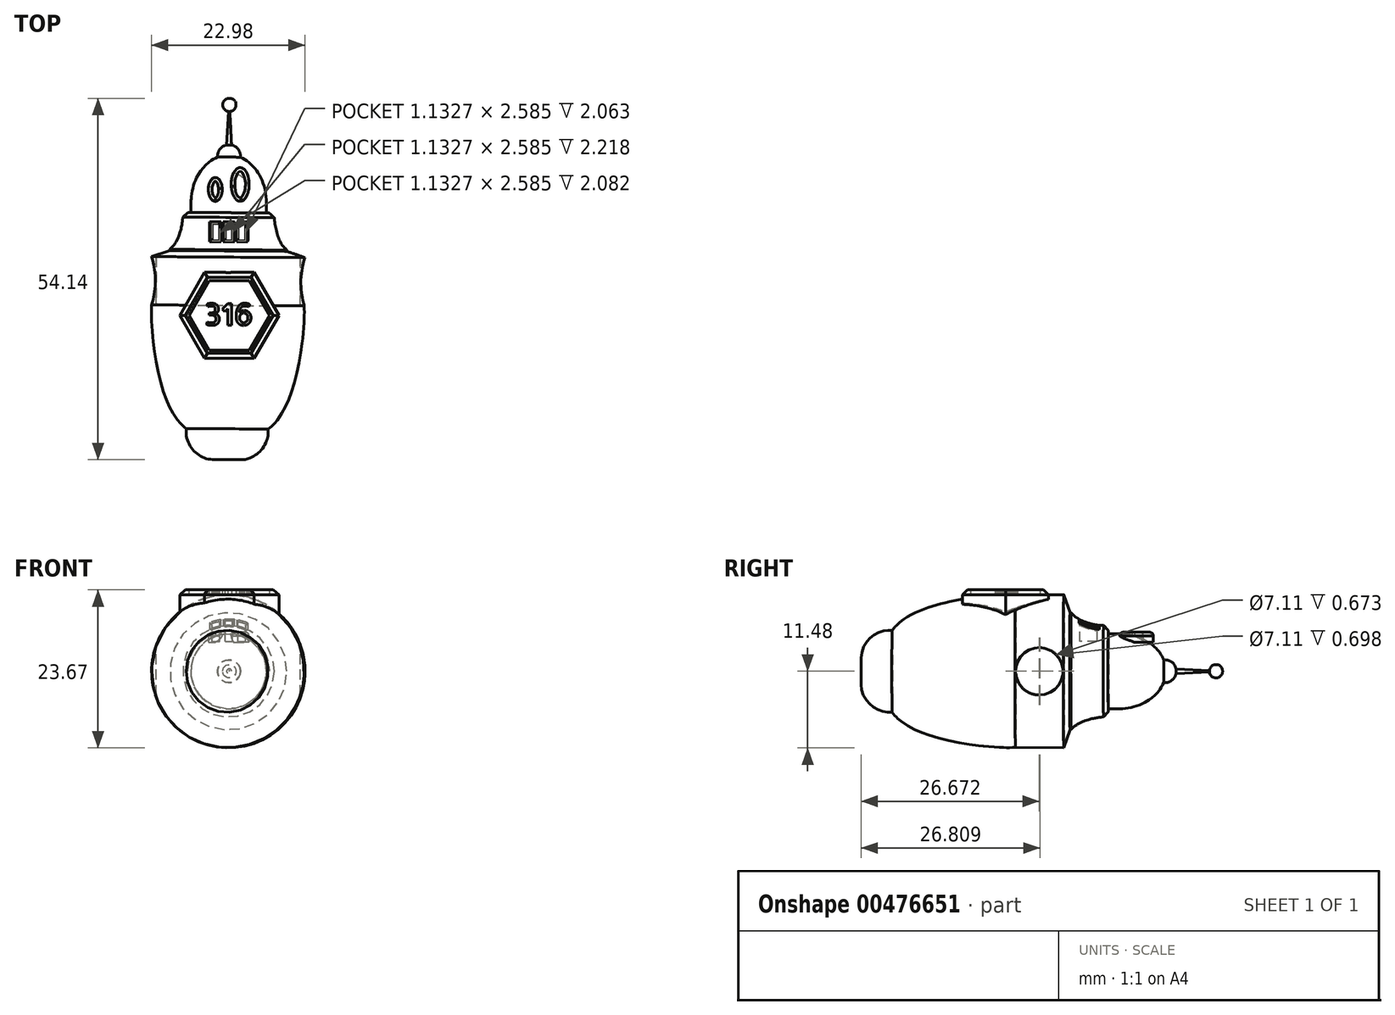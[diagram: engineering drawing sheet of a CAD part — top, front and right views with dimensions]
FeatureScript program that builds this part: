
annotation { "Feature Type Name" : "Feature", "Feature Type Description" : "" }
export const myFeature = defineFeature(function(context is Context, id is Id, definition is map)
    precondition{}
    {
        {
            var Q0;
            Q0=qCreatedBy(makeId("Top.planeOp"),FACE);
            var sketch = newSketch(context, id + "F0", { "sketchPlane" : qUnion([Q0])});
            skLineSegment(sketch, "E0", {"start": v(-10.48, 12.63) * mm, "end": v(-10.48, 19.87) * mm});
            skFitSpline(sketch, "E1", {"points": [v(10.09, 20.95) * mm, v(10.15, 21.01) * mm], "startDerivative": vector(0.06, 0.06) * mm, "endDerivative": vector(0.06, 0.06) * mm});
            skFitSpline(sketch, "E2", {"points": [v(-7.76, 20.95) * mm, v(-7.24, 21.45) * mm, v(-6.6, 22.5) * mm, v(-6.03, 24.25) * mm, v(-5.81, 25.75) * mm, v(-5.77, 26.5) * mm], "startDerivative": vector(3.3, 2.83) * mm, "endDerivative": vector(0.16, 4.27) * mm});
            skLineSegment(sketch, "E3", {"start": v(-10.48, 19.87) * mm, "end": v(-7.76, 20.79) * mm});
            skLineSegment(sketch, "E4", {"start": v(-7.76, 20.79) * mm, "end": v(-7.76, 20.95) * mm});
            skLineSegment(sketch, "E5", {"start": v(-5.77, 26.5) * mm, "end": v(-4.58, 26.5) * mm});
            skFitSpline(sketch, "E6", {"points": [v(-4.58, 26.5) * mm, v(-4.58, 27.5) * mm, v(-4.5, 29.13) * mm, v(-4, 31.1) * mm, v(-3.35, 32.38) * mm, v(-2.49, 33.48) * mm, v(-1.51, 34.3) * mm, v(-0.6, 34.79) * mm], "startDerivative": vector(0, 7.8) * mm, "endDerivative": vector(7.4, 3.58) * mm});
            skFitSpline(sketch, "E7", {"points": [v(-0.6, 34.79) * mm, v(-0.6, 35.1) * mm, v(-0.49, 35.58) * mm, v(-0.23, 36) * mm, v(0.1, 36.33) * mm, v(0.49, 36.52) * mm, v(0.75, 36.6) * mm], "startDerivative": vector(-0.1, 2.05) * mm, "endDerivative": vector(1.87, 0.4) * mm});
            skPoint(sketch, "E8.endSnap0", {"position": v(1.17, 21.6) * mm});
            skLineSegment(sketch, "E9", {"start": v(0.75, 36.6) * mm, "end": v(1.07, 41.6) * mm});
            skFitSpline(sketch, "E10", {"points": [v(1.07, 41.6) * mm, v(0.8, 41.67) * mm, v(0.53, 41.82) * mm, v(0.33, 42.03) * mm, v(0.2, 42.3) * mm, v(0.17, 42.5) * mm, v(0.16, 42.76) * mm, v(0.2, 42.94) * mm, v(0.31, 43.15) * mm, v(0.5, 43.35) * mm, v(0.66, 43.48) * mm, v(0.83, 43.54) * mm, v(1.04, 43.57) * mm, v(1.17, 43.57) * mm], "startDerivative": vector(-3.3, 0.6) * mm, "endDerivative": vector(2, -0.06) * mm});
            skFitSpline(sketch, "E11", {"points": [v(-10.48, 12.63) * mm, v(-10.48, 10.12) * mm, v(-10.15, 6.52) * mm, v(-9.38, 2.07) * mm, v(-7.68, -2.9) * mm, v(-6, -5.3) * mm, v(-5.29, -5.89) * mm], "startDerivative": vector(-0.37, -16.05) * mm, "endDerivative": vector(7.16, -5.3) * mm});
            skFitSpline(sketch, "E12", {"points": [v(-5.29, -5.89) * mm, v(-5.29, -6.9) * mm, v(-4.86, -8.2) * mm, v(-4.1, -9.28) * mm, v(-3.04, -10.07) * mm, v(-1.85, -10.48) * mm, v(-0.47, -10.54) * mm, v(0.8, -10.54) * mm], "startDerivative": vector(-0.6, -7.63) * mm, "endDerivative": vector(8.74, -0.05) * mm});
            skLineSegment(sketch, "E13", {"start": v(0.8, -10.54) * mm, "end": v(1.17, 43.57) * mm});
            skSolve(sketch);
        }
        {
            var Q0;
            Q0 = qSketchRegion(id + "F0", true);
            var Q1;
            Q1=sQuery(id+"F0.wireOp",EDGE,"E13");
            revolve(context, id + "F1", {"entities" : qUnion([Q0]), "axis" : qUnion([Q1]), "revolveType" : RevolveType.FULL});
        }
        {
            var Q0;
            Q0=qCreatedBy(makeId("Top.planeOp"),FACE);
            var Q1;
            Q1 = qBodyType(qCreatedBy(id + "F3" ,EDGE), BodyType.WIRE);
            cPlane(context, id + "F2", {"entities" : qUnion([Q0, Q1]), "cplaneType" : CPlaneType.OFFSET, "offset" : 5.08 * mm, "width" : 152.4 * mm, "height" : 152.4 * mm});
        }
        {
            var Q0;
            Q0=qCreatedBy(id+"F2.planeOp",FACE);
            var sketch = newSketch(context, id + "F3", { "sketchPlane" : qUnion([Q0])});
            skEllipse(sketch, "E14", {"center": v(-0.95, 29.94) * mm, "majorRadius": 1.78 * mm, "minorRadius": 1.04 * mm, "majorAxis": v(0, -1)});
            skEllipse(sketch, "E15", {"center": v(2.78, 30.68) * mm, "majorRadius": 2.53 * mm, "minorRadius": 1.34 * mm, "majorAxis": v(0, 1)});
            skPoint(sketch, "E16.endSnap0", {"position": v(-0.95, 28.16) * mm});
            skSolve(sketch);
        }
        {
            var Q0;
            Q0 = qSketchRegion(id + "F3", true);
            extrude(context, id + "F4", {"entities" : qUnion([Q0]), "operationType" : NewBodyOperationType.ADD, "endBound" : BoundingType.SYMMETRIC, "depth" : 1.52 * mm});
        }
        {
            var Q0;
            Q0=makeQuery(id+"F4.opExtrude","CAP_EDGE",EDGE,{"disambiguationData":[OSD([sQuery(id+"F3.wireOp",EDGE,"E15")])],"isStart":false});
            var Q1;
            Q1=makeQuery(id+"F4.opExtrude","CAP_EDGE",EDGE,{"disambiguationData":[OSD([sQuery(id+"F3.wireOp",EDGE,"E14")])],"isStart":false});
            fillet(context, id + "F5", {"entities" : qUnion([Q0, Q1]), "radius" : 0.55 * mm, "tangentPropagation" : true, "allowEdgeOverflow" : false});
        }
        {
            var Q0;
            Q0=qCreatedBy(makeId("Top.planeOp"),FACE);
            cPlane(context, id + "F6", {"entities" : qUnion([Q0]), "cplaneType" : CPlaneType.OFFSET, "offset" : 6.35 * mm, "width" : 152.4 * mm, "height" : 152.4 * mm});
        }
        {
            var Q0;
            Q0=qCreatedBy(id+"F6.planeOp",FACE);
            var sketch = newSketch(context, id + "F7", { "sketchPlane" : qUnion([Q0])});
            skLineSegment(sketch, "E17.bottom", {"start": v(-1.44, 24.82) * mm, "end": v(-0.31, 24.82) * mm});
            skLineSegment(sketch, "E17.top", {"start": v(-1.44, 22.23) * mm, "end": v(-0.31, 22.23) * mm});
            skLineSegment(sketch, "E17.left", {"start": v(-1.44, 24.82) * mm, "end": v(-1.44, 22.23) * mm});
            skLineSegment(sketch, "E17.right", {"start": v(-0.31, 24.82) * mm, "end": v(-0.31, 22.23) * mm});
            skLineSegment(sketch, "E18.1.0.0", {"start": v(1.65, 24.82) * mm, "end": v(1.65, 22.23) * mm});
            skLineSegment(sketch, "E18.1.0.1", {"start": v(0.51, 24.82) * mm, "end": v(1.65, 24.82) * mm});
            skLineSegment(sketch, "E18.1.0.2", {"start": v(0.51, 24.82) * mm, "end": v(0.51, 22.23) * mm});
            skLineSegment(sketch, "E18.1.0.3", {"start": v(0.51, 22.23) * mm, "end": v(1.65, 22.23) * mm});
            skLineSegment(sketch, "E18.2.0.0", {"start": v(3.6, 24.82) * mm, "end": v(3.6, 22.23) * mm});
            skLineSegment(sketch, "E18.2.0.1", {"start": v(2.47, 24.82) * mm, "end": v(3.6, 24.82) * mm});
            skLineSegment(sketch, "E18.2.0.2", {"start": v(2.47, 24.82) * mm, "end": v(2.47, 22.23) * mm});
            skLineSegment(sketch, "E18.2.0.3", {"start": v(2.47, 22.23) * mm, "end": v(3.6, 22.23) * mm});
            skLineSegment(sketch, "E18.direction1", {"start": v(-0.31, 22.23) * mm, "end": v(1.65, 22.23) * mm, "construction": true});
            skSolve(sketch);
        }
        {
            var Q0;
            Q0 = qSketchRegion(id + "F7", true);
            extrude(context, id + "F8", {"entities" : qUnion([Q0]), "operationType" : NewBodyOperationType.REMOVE, "endBound" : BoundingType.SYMMETRIC, "oppositeDirection" : true, "depth" : 3.8 * mm});
        }
        {
            var Q0;
            Q0=qCreatedBy(makeId("Top.planeOp"),FACE);
            cPlane(context, id + "F9", {"entities" : qUnion([Q0]), "cplaneType" : CPlaneType.OFFSET, "offset" : 7.62 * mm, "width" : 152.4 * mm, "height" : 152.4 * mm});
        }
        {
            var Q0;
            Q0=qCreatedBy(id+"F9.planeOp",FACE);
            var sketch = newSketch(context, id + "F10", { "sketchPlane" : qUnion([Q0])});
            skCircle(sketch, "E19.cCircle", {"center": v(1.17, 11.07) * mm, "radius": 6.45 * mm, "construction": true});
            skLineSegment(sketch, "E19.0", {"start": v(-2.55, 17.52) * mm, "end": v(4.9, 17.52) * mm});
            skLineSegment(sketch, "E19.1", {"start": v(4.9, 17.52) * mm, "end": v(8.61, 11.07) * mm});
            skLineSegment(sketch, "E19.2", {"start": v(8.61, 11.07) * mm, "end": v(4.9, 4.62) * mm});
            skLineSegment(sketch, "E19.3", {"start": v(4.9, 4.62) * mm, "end": v(-2.55, 4.62) * mm});
            skLineSegment(sketch, "E19.4", {"start": v(-2.55, 4.62) * mm, "end": v(-6.28, 11.07) * mm});
            skLineSegment(sketch, "E19.5", {"start": v(-6.28, 11.07) * mm, "end": v(-2.55, 17.52) * mm});
            skPoint(sketch, "E19.0.midPoint", {"position": v(1.17, 17.52) * mm});
            skSolve(sketch);
        }
        {
            var Q0;
            Q0 = qSketchRegion(id + "F10", true);
            extrude(context, id + "F11", {"entities" : qUnion([Q0]), "operationType" : NewBodyOperationType.ADD, "depth" : 4.57 * mm});
        }
        {
            var Q0;
            Q0=makeQuery(id+"F11.opExtrude","CAP_FACE",FACE,{"disambiguationData":[OSD([sQuery(id+"F10.wireOp",EDGE,"E19.0"),sQuery(id+"F10.wireOp",EDGE,"E19.1"),sQuery(id+"F10.wireOp",EDGE,"E19.2"),sQuery(id+"F10.wireOp",EDGE,"E19.3"),sQuery(id+"F10.wireOp",EDGE,"E19.4"),sQuery(id+"F10.wireOp",EDGE,"E19.5")])],"isStart":false});
            var sketch = newSketch(context, id + "F12", { "sketchPlane" : qUnion([Q0])});
            skCircle(sketch, "E20.cCircle", {"center": v(1.17, 11.07) * mm, "radius": 5.21 * mm, "construction": true});
            skPoint(sketch, "E20.cCircle.centerSnap0", {"position": v(1.17, 17.52) * mm});
            skLineSegment(sketch, "E20.0", {"start": v(-1.84, 16.28) * mm, "end": v(4.18, 16.28) * mm});
            skLineSegment(sketch, "E20.1", {"start": v(4.18, 16.28) * mm, "end": v(7.19, 11.07) * mm});
            skLineSegment(sketch, "E20.2", {"start": v(7.19, 11.07) * mm, "end": v(4.18, 5.86) * mm});
            skLineSegment(sketch, "E20.3", {"start": v(4.18, 5.86) * mm, "end": v(-1.84, 5.86) * mm});
            skLineSegment(sketch, "E20.4", {"start": v(-1.84, 5.86) * mm, "end": v(-4.85, 11.07) * mm});
            skLineSegment(sketch, "E20.5", {"start": v(-4.85, 11.07) * mm, "end": v(-1.84, 16.28) * mm});
            skPoint(sketch, "E20.0.midPoint", {"position": v(1.17, 16.28) * mm});
            skSolve(sketch);
        }
        {
            var Q0;
            Q0 = qSketchRegion(id + "F12", true);
            extrude(context, id + "F13", {"entities" : qUnion([Q0]), "operationType" : NewBodyOperationType.REMOVE, "oppositeDirection" : true, "depth" : 0.76 * mm});
        }
        {
            var Q0;
            Q0=makeQuery(id+"F11.opExtrude","CAP_EDGE",EDGE,{"disambiguationData":[OSD([sQuery(id+"F10.wireOp",EDGE,"E19.5")])],"isStart":false});
            var Q1;
            Q1=makeQuery(id+"F11.opExtrude","CAP_EDGE",EDGE,{"disambiguationData":[OSD([sQuery(id+"F10.wireOp",EDGE,"E19.4")])],"isStart":false});
            var Q2;
            Q2=makeQuery(id+"F11.opExtrude","CAP_EDGE",EDGE,{"disambiguationData":[OSD([sQuery(id+"F10.wireOp",EDGE,"E19.3")])],"isStart":false});
            var Q3;
            Q3=makeQuery(id+"F11.opExtrude","CAP_EDGE",EDGE,{"disambiguationData":[OSD([sQuery(id+"F10.wireOp",EDGE,"E19.0")])],"isStart":false});
            var Q4;
            Q4=makeQuery(id+"F11.opExtrude","CAP_EDGE",EDGE,{"disambiguationData":[OSD([sQuery(id+"F10.wireOp",EDGE,"E19.1")])],"isStart":false});
            var Q5;
            Q5=makeQuery(id+"F11.opExtrude","CAP_EDGE",EDGE,{"disambiguationData":[OSD([sQuery(id+"F10.wireOp",EDGE,"E19.2")])],"isStart":false});
            chamfer(context, id + "F14", {"entities" : qUnion([Q0, Q1, Q2, Q3, Q4, Q5]), "width" : 0.76 * mm, "tangentPropagation" : true});
        }
        {
            var Q0;
            Q0=makeQuery(id+"F13.boolean.opBoolean","COPY",FACE,{"derivedFrom":makeQuery(id+"F13.opExtrude","CAP_FACE",FACE,{"disambiguationData":[OSD([sQuery(id+"F12.wireOp",EDGE,"E20.0"),sQuery(id+"F12.wireOp",EDGE,"E20.1"),sQuery(id+"F12.wireOp",EDGE,"E20.2"),sQuery(id+"F12.wireOp",EDGE,"E20.3"),sQuery(id+"F12.wireOp",EDGE,"E20.4"),sQuery(id+"F12.wireOp",EDGE,"E20.5")])],"isStart":false})});
            var sketch = newSketch(context, id + "F15", { "sketchPlane" : qUnion([Q0])});
            skText(sketch, "E21", { "text": "316", "fontName": "AllertaStencil-Regular.ttf"});
            const initialGuessF15  = {"E21": [-0.0026, 0.00958, 1, 0, 0.00328]};
            skSetInitialGuess(sketch, initialGuessF15);
            skSolve(sketch);
        }
        {
            var Q0;
            Q0 = qSketchRegion(id + "F15", true);
            extrude(context, id + "F16", {"entities" : qUnion([Q0]), "operationType" : NewBodyOperationType.ADD, "depth" : 0.76 * mm});
        }
        {
            var Q0;
            Q0=makeQuery(id+"F8.boolean.opBoolean","INTERSECT",EDGE,{"derivedFrom":[makeQuery(id+"F1.opRevolve","SWEPT_FACE",FACE,{"disambiguationData":[OSD([sQuery(id+"F0.wireOp",EDGE,"E2")])]}),makeQuery(id+"F8.opExtrude","SWEPT_FACE",FACE,{"disambiguationData":[OSD([sQuery(id+"F7.wireOp",EDGE,"E17.bottom")])]})]});
            var Q1;
            Q1=makeQuery(id+"F8.boolean.opBoolean","INTERSECT",EDGE,{"derivedFrom":[makeQuery(id+"F1.opRevolve","SWEPT_FACE",FACE,{"disambiguationData":[OSD([sQuery(id+"F0.wireOp",EDGE,"E2")])]}),makeQuery(id+"F8.opExtrude","SWEPT_FACE",FACE,{"disambiguationData":[OSD([sQuery(id+"F7.wireOp",EDGE,"E17.right")])]})]});
            var Q2;
            Q2=makeQuery(id+"F8.boolean.opBoolean","INTERSECT",EDGE,{"derivedFrom":[makeQuery(id+"F1.opRevolve","SWEPT_FACE",FACE,{"disambiguationData":[OSD([sQuery(id+"F0.wireOp",EDGE,"E2")])]}),makeQuery(id+"F8.opExtrude","SWEPT_FACE",FACE,{"disambiguationData":[OSD([sQuery(id+"F7.wireOp",EDGE,"E17.top")])]})]});
            var Q3;
            Q3=makeQuery(id+"F8.boolean.opBoolean","INTERSECT",EDGE,{"derivedFrom":[makeQuery(id+"F1.opRevolve","SWEPT_FACE",FACE,{"disambiguationData":[OSD([sQuery(id+"F0.wireOp",EDGE,"E2")])]}),makeQuery(id+"F8.opExtrude","SWEPT_FACE",FACE,{"disambiguationData":[OSD([sQuery(id+"F7.wireOp",EDGE,"E17.left")])]})]});
            var Q4;
            Q4=makeQuery(id+"F8.boolean.opBoolean","INTERSECT",EDGE,{"derivedFrom":[makeQuery(id+"F1.opRevolve","SWEPT_FACE",FACE,{"disambiguationData":[OSD([sQuery(id+"F0.wireOp",EDGE,"E2")])]}),makeQuery(id+"F8.opExtrude","SWEPT_FACE",FACE,{"disambiguationData":[OSD([sQuery(id+"F7.wireOp",EDGE,"E18.1.0.1")])]})]});
            var Q5;
            Q5=makeQuery(id+"F8.boolean.opBoolean","INTERSECT",EDGE,{"derivedFrom":[makeQuery(id+"F1.opRevolve","SWEPT_FACE",FACE,{"disambiguationData":[OSD([sQuery(id+"F0.wireOp",EDGE,"E2")])]}),makeQuery(id+"F8.opExtrude","SWEPT_FACE",FACE,{"disambiguationData":[OSD([sQuery(id+"F7.wireOp",EDGE,"E18.1.0.2")])]})]});
            var Q6;
            Q6=makeQuery(id+"F8.boolean.opBoolean","INTERSECT",EDGE,{"derivedFrom":[makeQuery(id+"F1.opRevolve","SWEPT_FACE",FACE,{"disambiguationData":[OSD([sQuery(id+"F0.wireOp",EDGE,"E2")])]}),makeQuery(id+"F8.opExtrude","SWEPT_FACE",FACE,{"disambiguationData":[OSD([sQuery(id+"F7.wireOp",EDGE,"E18.1.0.3")])]})]});
            var Q7;
            Q7=makeQuery(id+"F8.boolean.opBoolean","INTERSECT",EDGE,{"derivedFrom":[makeQuery(id+"F1.opRevolve","SWEPT_FACE",FACE,{"disambiguationData":[OSD([sQuery(id+"F0.wireOp",EDGE,"E2")])]}),makeQuery(id+"F8.opExtrude","SWEPT_FACE",FACE,{"disambiguationData":[OSD([sQuery(id+"F7.wireOp",EDGE,"E18.1.0.0")])]})]});
            var Q8;
            Q8=makeQuery(id+"F8.boolean.opBoolean","INTERSECT",EDGE,{"derivedFrom":[makeQuery(id+"F1.opRevolve","SWEPT_FACE",FACE,{"disambiguationData":[OSD([sQuery(id+"F0.wireOp",EDGE,"E2")])]}),makeQuery(id+"F8.opExtrude","SWEPT_FACE",FACE,{"disambiguationData":[OSD([sQuery(id+"F7.wireOp",EDGE,"E18.2.0.2")])]})]});
            var Q9;
            Q9=makeQuery(id+"F8.boolean.opBoolean","INTERSECT",EDGE,{"derivedFrom":[makeQuery(id+"F1.opRevolve","SWEPT_FACE",FACE,{"disambiguationData":[OSD([sQuery(id+"F0.wireOp",EDGE,"E2")])]}),makeQuery(id+"F8.opExtrude","SWEPT_FACE",FACE,{"disambiguationData":[OSD([sQuery(id+"F7.wireOp",EDGE,"E18.2.0.1")])]})]});
            var Q10;
            Q10=makeQuery(id+"F8.boolean.opBoolean","INTERSECT",EDGE,{"derivedFrom":[makeQuery(id+"F1.opRevolve","SWEPT_FACE",FACE,{"disambiguationData":[OSD([sQuery(id+"F0.wireOp",EDGE,"E2")])]}),makeQuery(id+"F8.opExtrude","SWEPT_FACE",FACE,{"disambiguationData":[OSD([sQuery(id+"F7.wireOp",EDGE,"E18.2.0.0")])]})]});
            var Q11;
            Q11=makeQuery(id+"F8.boolean.opBoolean","INTERSECT",EDGE,{"derivedFrom":[makeQuery(id+"F1.opRevolve","SWEPT_FACE",FACE,{"disambiguationData":[OSD([sQuery(id+"F0.wireOp",EDGE,"E2")])]}),makeQuery(id+"F8.opExtrude","SWEPT_FACE",FACE,{"disambiguationData":[OSD([sQuery(id+"F7.wireOp",EDGE,"E18.2.0.3")])]})]});
            chamfer(context, id + "F17", {"entities" : qUnion([Q0, Q1, Q2, Q3, Q4, Q5, Q6, Q7, Q8, Q9, Q10, Q11]), "width" : 0.25 * mm, "tangentPropagation" : true});
        }
        {
            var Q0;
            Q0=qCreatedBy(makeId("Right.planeOp"),FACE);
            cPlane(context, id + "F18", {"entities" : qUnion([Q0]), "cplaneType" : CPlaneType.OFFSET, "offset" : 12.45 * mm, "width" : 152.4 * mm, "height" : 152.4 * mm});
        }
        {
            var Q0;
            Q0=qCreatedBy(id+"F18.planeOp",FACE);
            var sketch = newSketch(context, id + "F19", { "sketchPlane" : qUnion([Q0])});
            skCircle(sketch, "E22", {"center": v(16.11, 0) * mm, "radius": 3.56 * mm});
            skSolve(sketch);
        }
        {
            var Q0;
            Q0 = qSketchRegion(id + "F19", true);
            extrude(context, id + "F20", {"entities" : qUnion([Q0]), "operationType" : NewBodyOperationType.REMOVE, "endBound" : BoundingType.SYMMETRIC, "oppositeDirection" : true, "depth" : 1.27 * mm});
        }
        {
            var Q0;
            Q0=qCreatedBy(makeId("Right.planeOp"),FACE);
            cPlane(context, id + "F21", {"entities" : qUnion([Q0]), "cplaneType" : CPlaneType.OFFSET, "offset" : 10.4 * mm, "oppositeDirection" : true, "width" : 152.4 * mm, "height" : 152.4 * mm});
        }
        {
            var Q0;
            Q0=qCreatedBy(id+"F21.planeOp",FACE);
            var sketch = newSketch(context, id + "F22", { "sketchPlane" : qUnion([Q0])});
            skCircle(sketch, "E23", {"center": v(16.25, 0) * mm, "radius": 3.56 * mm});
            skSolve(sketch);
        }
        {
            var Q0;
            Q0 = qSketchRegion(id + "F22", true);
            extrude(context, id + "F23", {"entities" : qUnion([Q0]), "operationType" : NewBodyOperationType.REMOVE, "endBound" : BoundingType.SYMMETRIC, "oppositeDirection" : true, "depth" : 1.27 * mm});
        }
        {
            var Q0;
            Q0=makeQuery(id+"F1.opRevolve","SWEPT_EDGE",EDGE,{"disambiguationData":[OSD([sQuery(id+"F0.wireOp",EDGE,"E2"),sQuery(id+"F0.wireOp",EDGE,"E5")])]});
            chamfer(context, id + "F24", {"entities" : qUnion([Q0]), "width" : 0.76 * mm, "tangentPropagation" : true});
        }
    });
